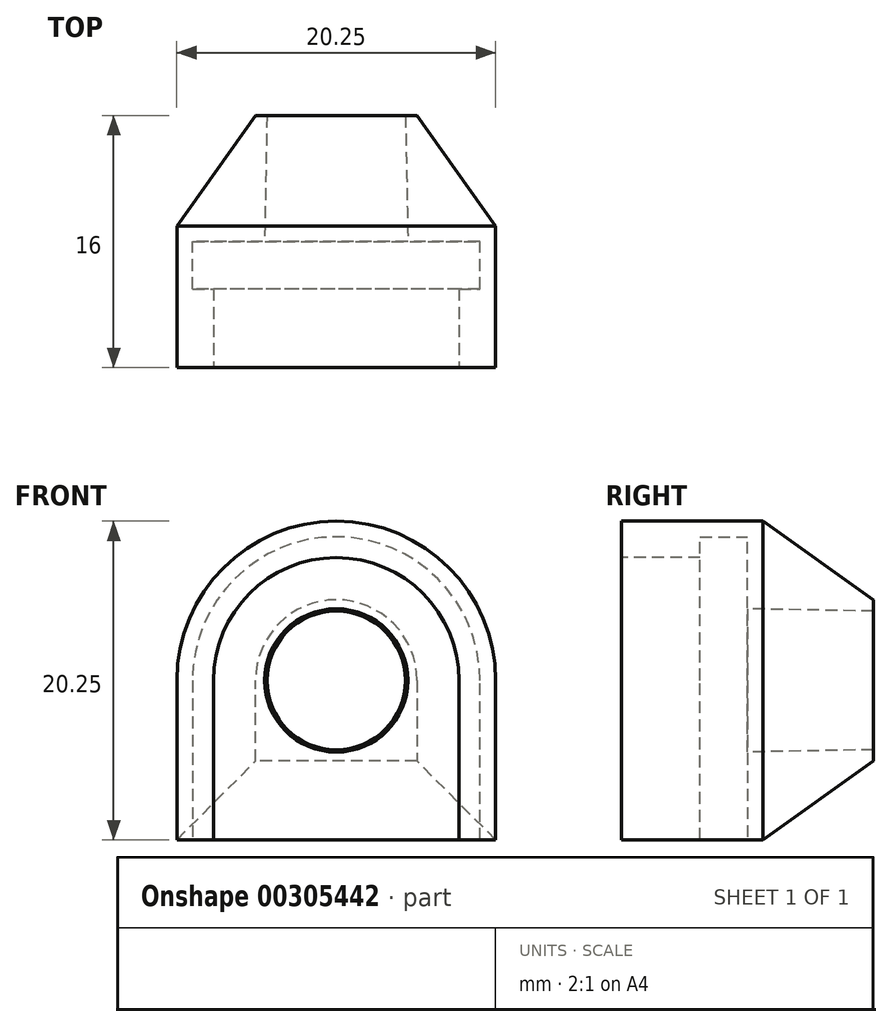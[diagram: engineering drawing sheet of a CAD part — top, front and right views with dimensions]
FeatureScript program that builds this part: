
annotation { "Feature Type Name" : "Feature", "Feature Type Description" : "" }
export const myFeature = defineFeature(function(context is Context, id is Id, definition is map)
    precondition{}
    {
        {
            var Q0;
            Q0=qCreatedBy(makeId("Top.planeOp"),FACE);
            var sketch = newSketch(context, id + "F0", { "sketchPlane" : qUnion([Q0])});
            skArc(sketch, "E0", {"start": v(-10.13, 0) * mm, "mid": v(0, 10.13) * mm, "end": v(10.13, 0) * mm});
            skLineSegment(sketch, "E1", {"start": v(-10.12, 0) * mm, "end": v(-10.13, -10.13) * mm});
            skLineSegment(sketch, "E2", {"start": v(-10.12, -10.13) * mm, "end": v(10.12, -10.13) * mm});
            skLineSegment(sketch, "E3", {"start": v(10.12, -10.13) * mm, "end": v(10.12, 0) * mm});
            skSolve(sketch);
        }
        {
            var Q0;
            Q0 = qSketchRegion(id + "F0", true);
            extrude(context, id + "F1", {"entities" : qUnion([Q0]), "depth" : 16 * mm});
        }
        {
            var Q0;
            Q0=makeQuery(id+"F1.opExtrude","CAP_FACE",FACE,{"disambiguationData":[OSD([sQuery(id+"F0.wireOp",EDGE,"E0"),sQuery(id+"F0.wireOp",EDGE,"E1"),sQuery(id+"F0.wireOp",EDGE,"E2"),sQuery(id+"F0.wireOp",EDGE,"E3")])],"isStart":false});
            var sketch = newSketch(context, id + "F2", { "sketchPlane" : qUnion([Q0])});
            skArc(sketch, "E4", {"start": v(-7.8, 0) * mm, "mid": v(0, 7.8) * mm, "end": v(7.8, 0) * mm});
            skLineSegment(sketch, "E5", {"start": v(-7.8, 0) * mm, "end": v(-7.8, -10.13) * mm});
            skLineSegment(sketch, "E6", {"start": v(-7.8, -10.13) * mm, "end": v(7.8, -10.13) * mm});
            skLineSegment(sketch, "E7", {"start": v(7.8, -10.13) * mm, "end": v(7.8, 0) * mm});
            skSolve(sketch);
        }
        {
            var Q0;
            Q0 = qSketchRegion(id + "F2", true);
            extrude(context, id + "F3", {"entities" : qUnion([Q0]), "operationType" : NewBodyOperationType.REMOVE, "oppositeDirection" : true, "depth" : 8 * mm});
        }
        {
            var Q0;
            Q0=makeQuery(id+"F3.boolean.opBoolean","COPY",FACE,{"derivedFrom":makeQuery(id+"F3.opExtrude","CAP_FACE",FACE,{"disambiguationData":[OSD([sQuery(id+"F2.wireOp",EDGE,"E4"),sQuery(id+"F2.wireOp",EDGE,"E5"),sQuery(id+"F2.wireOp",EDGE,"E6"),sQuery(id+"F2.wireOp",EDGE,"E7")])],"isStart":false})});
            var sketch = newSketch(context, id + "F4", { "sketchPlane" : qUnion([Q0])});
            skArc(sketch, "E8", {"start": v(-9.12, 0) * mm, "mid": v(0, 9.12) * mm, "end": v(9.12, 0) * mm});
            skLineSegment(sketch, "E9", {"start": v(-9.12, 0) * mm, "end": v(-9.12, -10.13) * mm});
            skLineSegment(sketch, "E10", {"start": v(-9.12, -10.13) * mm, "end": v(9.12, -10.13) * mm});
            skLineSegment(sketch, "E11", {"start": v(9.12, -10.13) * mm, "end": v(9.12, 0) * mm});
            skSolve(sketch);
        }
        {
            var Q0;
            Q0 = qSketchRegion(id + "F4", true);
            extrude(context, id + "F5", {"entities" : qUnion([Q0]), "operationType" : NewBodyOperationType.REMOVE, "depth" : 3 * mm});
        }
        {
            var Q0;
            Q0=makeQuery(id+"F5.boolean.opBoolean","MERGE",FACE,{"derivedFrom":[makeQuery(id+"F3.boolean.opBoolean","COPY",FACE,{"derivedFrom":makeQuery(id+"F3.opExtrude","CAP_FACE",FACE,{"disambiguationData":[OSD([sQuery(id+"F2.wireOp",EDGE,"E4"),sQuery(id+"F2.wireOp",EDGE,"E5"),sQuery(id+"F2.wireOp",EDGE,"E6"),sQuery(id+"F2.wireOp",EDGE,"E7")])],"isStart":false})}),makeQuery(id+"F5.opExtrude","CAP_FACE",FACE,{"disambiguationData":[OSD([sQuery(id+"F4.wireOp",EDGE,"E8"),sQuery(id+"F4.wireOp",EDGE,"E9"),sQuery(id+"F4.wireOp",EDGE,"E10"),sQuery(id+"F4.wireOp",EDGE,"E11")])],"isStart":true})]});
            var sketch = newSketch(context, id + "F6", { "sketchPlane" : qUnion([Q0])});
            skCircle(sketch, "E12", {"center": v(0, 0) * mm, "radius": 4.55 * mm});
            skSolve(sketch);
        }
        {
            var Q0;
            Q0=makeQuery(id+"F1.opExtrude","CAP_FACE",FACE,{"disambiguationData":[OSD([sQuery(id+"F0.wireOp",EDGE,"E0"),sQuery(id+"F0.wireOp",EDGE,"E1"),sQuery(id+"F0.wireOp",EDGE,"E2"),sQuery(id+"F0.wireOp",EDGE,"E3")])],"isStart":true});
            var sketch = newSketch(context, id + "F7", { "sketchPlane" : qUnion([Q0])});
            skCircle(sketch, "E13", {"center": v(0, 0) * mm, "radius": 4.4 * mm});
            skSolve(sketch);
        }
        {
            var Q1;
            Q1=makeQuery(id+"F7.imprint","IMPRINT",FACE,{"disambiguationData":[TD([[makeQuery(id+"F7.imprint","IMPRINT",EDGE,{"derivedFrom":sQuery(id+"F7.wireOp",EDGE,"E13")}),1.0]])]});
            var Q2;
            Q2=makeQuery(id+"F6.imprint","IMPRINT",FACE,{"disambiguationData":[TD([[makeQuery(id+"F6.imprint","IMPRINT",EDGE,{"derivedFrom":sQuery(id+"F6.wireOp",EDGE,"E12")}),1.0]])]});
            loft(context, id + "F8", {"operationType" : NewBodyOperationType.REMOVE, "sheetProfilesArray" : [{ "sheetProfileEntities" : qUnion([Q1]) }, { "sheetProfileEntities" : qUnion([Q2]) }]});
        }
        {
            var Q0;
            Q0=makeQuery(id+"F1.opExtrude","SWEPT_BODY",BODY,{"disambiguationData":[OSD([sQuery(id+"F0.wireOp",EDGE,"E0"),sQuery(id+"F0.wireOp",EDGE,"E1"),sQuery(id+"F0.wireOp",EDGE,"E2"),sQuery(id+"F0.wireOp",EDGE,"E3")])]});
            var Q1;
            Q1=makeQuery(id+"F1.opExtrude","CAP_EDGE",EDGE,{"disambiguationData":[OSD([sQuery(id+"F0.wireOp",EDGE,"E2")])],"isStart":true});
            transform(context, id + "F9", {"entities" : qUnion([Q0]), "transformType" : TransformType.ROTATION, "transformAxis" : qUnion([Q1]), "angle" : 90 * degree, "makeCopy" : false});
        }
        {
            var Q0;
            Q0=makeQuery(id+"F1.opExtrude","CAP_EDGE",EDGE,{"disambiguationData":[OSD([sQuery(id+"F0.wireOp",EDGE,"E3")])],"isStart":true});
            var Q1;
            Q1=makeQuery(id+"F1.opExtrude","CAP_EDGE",EDGE,{"disambiguationData":[OSD([sQuery(id+"F0.wireOp",EDGE,"E0")])],"isStart":true});
            var Q2;
            Q2=makeQuery(id+"F1.opExtrude","CAP_EDGE",EDGE,{"disambiguationData":[OSD([sQuery(id+"F0.wireOp",EDGE,"E2")])],"isStart":true});
            chamfer(context, id + "F10", {"entities" : qUnion([Q0, Q1, Q2]), "chamferType" : ChamferType.TWO_OFFSETS, "width1" : 7 * mm, "oppositeDirection" : false, "width2" : 5 * mm, "tangentPropagation" : true});
        }
    });
